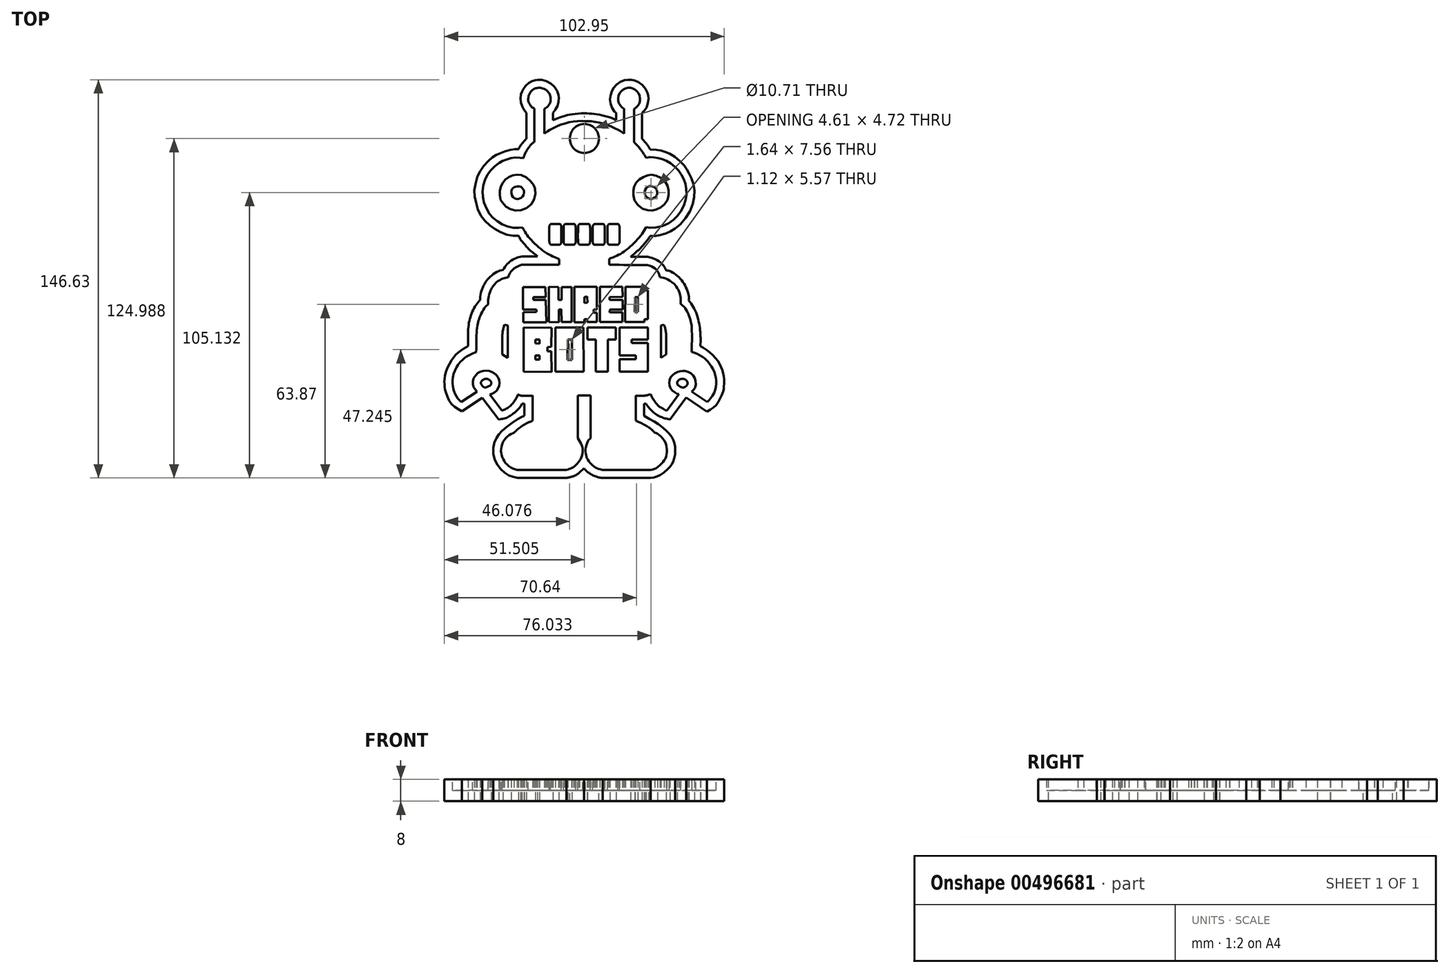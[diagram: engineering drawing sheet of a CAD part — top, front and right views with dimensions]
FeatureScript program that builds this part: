
annotation { "Feature Type Name" : "Feature", "Feature Type Description" : "" }
export const myFeature = defineFeature(function(context is Context, id is Id, definition is map)
    precondition{}
    {
        {
            var Q0;
            Q0=qCreatedBy(makeId("Top.planeOp"),FACE);
            var sketch = newSketch(context, id + "F0", { "sketchPlane" : qUnion([Q0])});
            skFitSpline(sketch, "E0", {"points": [v(-33.72, 61.57) * mm, v(-33.68, 52.13) * mm], "startDerivative": vector(0.03, -9.44) * mm, "endDerivative": vector(0.03, -9.44) * mm});
            skFitSpline(sketch, "E1", {"points": [v(-33.68, 52.13) * mm, v(-35.22, 50.28) * mm, v(-36.11, 49.12) * mm, v(-36.6, 48.2) * mm], "startDerivative": vector(-3.96, -4.75) * mm, "endDerivative": vector(-1.58, -3.42) * mm});
            skFitSpline(sketch, "E2", {"points": [v(-36.6, 48.2) * mm, v(-37.9, 48.2) * mm, v(-40.15, 47.82) * mm, v(-43.12, 46.8) * mm, v(-45.14, 45.9) * mm, v(-47.1, 44.4) * mm, v(-49.93, 41.25) * mm, v(-51.74, 37.9) * mm, v(-52.83, 32.84) * mm, v(-52.37, 29.1) * mm, v(-50.76, 24.21) * mm, v(-47.66, 20.53) * mm, v(-44.54, 18.3) * mm, v(-40, 16.5) * mm, v(-36.6, 16.26) * mm], "startDerivative": vector(-28.12, 1) * mm, "endDerivative": vector(46, 0.52) * mm});
            skFitSpline(sketch, "E3", {"points": [v(-36.6, 16.26) * mm, v(-35.5, 14.47) * mm, v(-34.14, 12.88) * mm, v(-32.5, 11.09) * mm, v(-30.32, 9.35) * mm, v(-29.6, 8.67) * mm], "startDerivative": vector(5.06, -9.07) * mm, "endDerivative": vector(4.26, -4.36) * mm});
            skFitSpline(sketch, "E4", {"points": [v(-29.6, 8.67) * mm, v(-31.14, 8.67) * mm, v(-35.06, 8.67) * mm, v(-37.67, 8) * mm, v(-40.33, 6.3) * mm, v(-42.36, 3.73) * mm], "startDerivative": vector(-9, -0.16) * mm, "endDerivative": vector(-8.6, -12.76) * mm});
            skFitSpline(sketch, "E5", {"points": [v(-42.36, 3.73) * mm, v(-44.44, 3.04) * mm, v(-47.3, 0.96) * mm, v(-49.03, -1.36) * mm, v(-50.24, -4.07) * mm, v(-50.73, -6.97) * mm, v(-50.68, -7.26) * mm], "startDerivative": vector(-12.18, -3) * mm, "endDerivative": vector(1.14, -3.42) * mm});
            skFitSpline(sketch, "E6", {"points": [v(-50.68, -7.26) * mm, v(-52.5, -9.64) * mm, v(-54.12, -13.1) * mm, v(-55, -16.96) * mm, v(-55.11, -24.3) * mm], "startDerivative": vector(-9.2, -10.68) * mm, "endDerivative": vector(0.5, -24.66) * mm});
            skFitSpline(sketch, "E7", {"points": [v(-55.11, -24.3) * mm, v(-56.92, -25.36) * mm, v(-59.18, -27.03) * mm, v(-61.34, -29.66) * mm, v(-63.32, -33.87) * mm, v(-63.85, -37.1) * mm, v(-63.8, -38.97) * mm, v(-63.4, -41.27) * mm, v(-61.31, -45.51) * mm, v(-57.37, -48.31) * mm], "startDerivative": vector(-19.75, -10.94) * mm, "endDerivative": vector(31.85, -17.11) * mm});
            skFitSpline(sketch, "E8", {"points": [v(-57.37, -48.31) * mm, v(-50, -43.37) * mm], "startDerivative": vector(7.38, 4.94) * mm, "endDerivative": vector(7.38, 4.94) * mm});
            skFitSpline(sketch, "E9", {"points": [v(-50, -43.37) * mm, v(-43.89, -51.34) * mm], "startDerivative": vector(6.1, -7.97) * mm, "endDerivative": vector(6.1, -7.97) * mm});
            skFitSpline(sketch, "E10", {"points": [v(-43.89, -51.34) * mm, v(-40.84, -50.63) * mm, v(-38.2, -48.92) * mm, v(-35.96, -46.73) * mm, v(-35.35, -45.59) * mm], "startDerivative": vector(11.52, 1.79) * mm, "endDerivative": vector(2.53, 6.09) * mm});
            skFitSpline(sketch, "E11", {"points": [v(-35.35, -45.59) * mm, v(-34.41, -45.59) * mm], "startDerivative": vector(0.94, 0) * mm, "endDerivative": vector(0.94, 0) * mm});
            skFitSpline(sketch, "E12", {"points": [v(-34.41, -45.59) * mm, v(-34.41, -49.94) * mm], "startDerivative": vector(0, -4.35) * mm, "endDerivative": vector(0, -4.35) * mm});
            skFitSpline(sketch, "E13", {"points": [v(-34.41, -49.94) * mm, v(-35.94, -50.7) * mm, v(-41.53, -54.53) * mm, v(-44.22, -57.38) * mm, v(-45.67, -60.78) * mm, v(-45.44, -65.99) * mm, v(-42.51, -70.27) * mm, v(-39.44, -72.24) * mm, v(-36.49, -72.85) * mm, v(-35.04, -72.87) * mm, v(-19, -72.9) * mm], "startDerivative": vector(-20.15, -8.85) * mm, "endDerivative": vector(109.37, -0.31) * mm});
            skFitSpline(sketch, "E14", {"points": [v(-19, -72.9) * mm, v(-16.81, -72.36) * mm, v(-14.75, -71.35) * mm, v(-12.5, -69.3) * mm], "startDerivative": vector(7.07, 1.43) * mm, "endDerivative": vector(6.04, 6.2) * mm});
            skFitSpline(sketch, "E15", {"points": [v(-12.5, -69.3) * mm, v(-11.55, -70.31) * mm, v(-9.99, -71.47) * mm, v(-7.7, -72.5) * mm, v(-5.6, -72.9) * mm], "startDerivative": vector(4.23, -4.86) * mm, "endDerivative": vector(8.02, -0.98) * mm});
            skFitSpline(sketch, "E16", {"points": [v(-5.6, -72.9) * mm, v(12, -72.9) * mm], "startDerivative": vector(17.59, 0) * mm, "endDerivative": vector(17.59, 0) * mm});
            skFitSpline(sketch, "E17", {"points": [v(12, -72.9) * mm, v(13.93, -72.44) * mm, v(16.53, -71.16) * mm, v(19.02, -68.89) * mm, v(19.85, -67.74) * mm, v(20.67, -65.87) * mm, v(21.1, -62.88) * mm, v(20.89, -60.42) * mm, v(20.14, -58.37) * mm, v(18.17, -55.8) * mm, v(16.29, -54.24) * mm, v(14.59, -52.95) * mm, v(9.59, -49.94) * mm], "startDerivative": vector(26.18, 5.02) * mm, "endDerivative": vector(-46.44, 26.77) * mm});
            skFitSpline(sketch, "E18", {"points": [v(9.59, -49.94) * mm, v(9.59, -45.59) * mm], "startDerivative": vector(0, 4.35) * mm, "endDerivative": vector(0, 4.35) * mm});
            skFitSpline(sketch, "E19", {"points": [v(9.59, -45.59) * mm, v(10.38, -45.59) * mm], "startDerivative": vector(0.8, 0) * mm, "endDerivative": vector(0.8, 0) * mm});
            skFitSpline(sketch, "E20", {"points": [v(10.38, -45.59) * mm, v(11.08, -46.61) * mm, v(13.17, -48.8) * mm, v(15.38, -50.2) * mm, v(17.16, -50.87) * mm, v(19.2, -51.37) * mm], "startDerivative": vector(3.81, -6.07) * mm, "endDerivative": vector(10.55, -2.4) * mm});
            skFitSpline(sketch, "E21", {"points": [v(19.2, -51.37) * mm, v(25.12, -43.29) * mm], "startDerivative": vector(5.91, 8.08) * mm, "endDerivative": vector(5.91, 8.08) * mm});
            skFitSpline(sketch, "E22", {"points": [v(25.12, -43.29) * mm, v(32.76, -48.49) * mm], "startDerivative": vector(7.65, -5.2) * mm, "endDerivative": vector(7.65, -5.2) * mm});
            skFitSpline(sketch, "E23", {"points": [v(32.76, -48.49) * mm, v(35.65, -46.46) * mm, v(37.6, -43.7) * mm, v(38.83, -40.77) * mm, v(39.01, -39.42) * mm, v(39.06, -36.24) * mm, v(38.63, -34.01) * mm, v(37.74, -31.54) * mm, v(35.98, -28.83) * mm, v(33.14, -26.03) * mm, v(30.37, -24.36) * mm], "startDerivative": vector(28.34, 17) * mm, "endDerivative": vector(-26.52, 14.03) * mm});
            skFitSpline(sketch, "E24", {"points": [v(30.37, -24.36) * mm, v(30.37, -20.16) * mm, v(29.9, -16.05) * mm, v(28.19, -10.73) * mm, v(26.07, -7.55) * mm], "startDerivative": vector(0.3, 17.5) * mm, "endDerivative": vector(-9.61, 12.23) * mm});
            skFitSpline(sketch, "E25", {"points": [v(26.07, -7.55) * mm, v(26.07, -5.66) * mm, v(24.63, -1.87) * mm, v(22.13, 1.31) * mm, v(19.2, 3.23) * mm, v(17.72, 3.6) * mm], "startDerivative": vector(1.13, 10.6) * mm, "endDerivative": vector(-9.43, 1.47) * mm});
            skFitSpline(sketch, "E26", {"points": [v(17.72, 3.6) * mm, v(17.06, 4.92) * mm, v(15.08, 6.92) * mm, v(11.67, 8.35) * mm, v(10.38, 8.57) * mm, v(4.7, 8.6) * mm], "startDerivative": vector(-3.75, 8.68) * mm, "endDerivative": vector(-24, -0.23) * mm});
            skFitSpline(sketch, "E27", {"points": [v(4.7, 8.6) * mm, v(8.33, 11.8) * mm, v(10.84, 14.7) * mm, v(12, 16.27) * mm], "startDerivative": vector(9.53, 7.9) * mm, "endDerivative": vector(4.11, 5.82) * mm});
            skFitSpline(sketch, "E28", {"points": [v(12, 16.27) * mm, v(14.18, 16.27) * mm, v(17.72, 17.14) * mm, v(20, 18.3) * mm, v(23.53, 21.05) * mm, v(27.23, 26.97) * mm, v(28.15, 31.96) * mm, v(27.59, 36.22) * mm, v(26.07, 39.36) * mm, v(25.12, 41.05) * mm, v(22.96, 43.62) * mm, v(19.57, 46.2) * mm, v(17.1, 47.25) * mm, v(15.35, 47.8) * mm, v(11.83, 48.08) * mm], "startDerivative": vector(35.37, -2.49) * mm, "endDerivative": vector(-53.89, 2.23) * mm});
            skFitSpline(sketch, "E29", {"points": [v(11.83, 48.08) * mm, v(10.9, 49.6) * mm, v(8.85, 52.07) * mm], "startDerivative": vector(-1.86, 3.4) * mm, "endDerivative": vector(-3.99, 4.5) * mm});
            skFitSpline(sketch, "E30", {"points": [v(8.85, 52.07) * mm, v(8.85, 61.58) * mm], "startDerivative": vector(0, 9.51) * mm, "endDerivative": vector(0, 9.51) * mm});
            skFitSpline(sketch, "E31", {"points": [v(8.85, 61.58) * mm, v(9.59, 62.28) * mm, v(10.69, 63.95) * mm, v(11.22, 66.73) * mm, v(11.22, 67.75) * mm, v(10.97, 68.74) * mm, v(9.83, 70.86) * mm, v(7.66, 72.83) * mm, v(5.86, 73.58) * mm, v(4.42, 73.7) * mm, v(2.84, 73.68) * mm, v(0.76, 72.86) * mm, v(-1.17, 71.27) * mm, v(-2.1, 70.02) * mm, v(-2.85, 67.54) * mm, v(-2.84, 65.4) * mm, v(-2.08, 63.3) * mm, v(-0.89, 61.67) * mm, v(-0.65, 61.48) * mm], "startDerivative": vector(16.73, 15) * mm, "endDerivative": vector(8.62, -5.35) * mm});
            skFitSpline(sketch, "E32", {"points": [v(-0.65, 61.48) * mm, v(-0.65, 58.88) * mm], "startDerivative": vector(0, -2.6) * mm, "endDerivative": vector(0, -2.6) * mm});
            skFitSpline(sketch, "E33", {"points": [v(-0.65, 58.88) * mm, v(-1.8, 59.48) * mm, v(-4.22, 60.26) * mm, v(-6.7, 60.81) * mm, v(-8.97, 61.15) * mm, v(-11.06, 61.32) * mm, v(-13.75, 61.32) * mm, v(-16.78, 61.07) * mm, v(-19, 60.62) * mm, v(-23.92, 58.88) * mm], "startDerivative": vector(-12.9, 7.75) * mm, "endDerivative": vector(-34.54, -13.03) * mm});
            skFitSpline(sketch, "E34", {"points": [v(-23.92, 58.88) * mm, v(-23.92, 61.58) * mm], "startDerivative": vector(0, 2.7) * mm, "endDerivative": vector(0, 2.7) * mm});
            skFitSpline(sketch, "E35", {"points": [v(-23.92, 61.58) * mm, v(-22.7, 63.16) * mm, v(-21.92, 65.13) * mm, v(-21.75, 67.33) * mm, v(-21.87, 68.1) * mm, v(-22.94, 70.58) * mm, v(-24.88, 72.48) * mm, v(-27.77, 73.67) * mm, v(-29.73, 73.69) * mm, v(-30.35, 73.62) * mm, v(-31.84, 73.14) * mm, v(-33.15, 72.27) * mm, v(-34.72, 70.52) * mm, v(-35.38, 69.24) * mm, v(-35.6, 68.66) * mm, v(-35.84, 66.9) * mm, v(-35.6, 64.8) * mm, v(-34.72, 63.02) * mm, v(-33.72, 61.57) * mm], "startDerivative": vector(22.48, 25.93) * mm, "endDerivative": vector(18.46, -25.37) * mm});
            skFitSpline(sketch, "E36", {"points": [v(-28.94, 70.8) * mm, v(-30.65, 70.45) * mm, v(-32.54, 68.64) * mm, v(-32.91, 65.76) * mm, v(-31.71, 63.71) * mm, v(-30.72, 63.16) * mm], "startDerivative": vector(-9.3, -0.64) * mm, "endDerivative": vector(6.7, -2.61) * mm});
            skFitSpline(sketch, "E37", {"points": [v(-30.72, 63.16) * mm, v(-30.72, 50.92) * mm], "startDerivative": vector(0, -12.24) * mm, "endDerivative": vector(0, -12.24) * mm});
            skFitSpline(sketch, "E38", {"points": [v(-30.72, 50.92) * mm, v(-32.35, 49.42) * mm, v(-34.41, 46.09) * mm, v(-34.72, 44.94) * mm], "startDerivative": vector(-4.79, -3.63) * mm, "endDerivative": vector(-0.65, -4.05) * mm});
            skFitSpline(sketch, "E39", {"points": [v(-34.72, 44.94) * mm, v(-36.25, 45.06) * mm, v(-38.34, 45.05) * mm, v(-40.14, 44.7) * mm, v(-42.23, 43.92) * mm, v(-43.5, 43.27) * mm, v(-45.77, 41.53) * mm, v(-47.97, 38.8) * mm, v(-49.35, 35.75) * mm, v(-49.76, 32.17) * mm, v(-49.38, 28.88) * mm, v(-47.65, 25.05) * mm, v(-45.87, 22.78) * mm, v(-43.1, 20.82) * mm, v(-40.08, 19.59) * mm, v(-36.8, 19.18) * mm, v(-35.1, 19.36) * mm], "startDerivative": vector(-30.9, 2.83) * mm, "endDerivative": vector(31.04, 5) * mm});
            skFitSpline(sketch, "E40", {"points": [v(-35.1, 19.36) * mm, v(-34.1, 17.54) * mm, v(-32.76, 15.62) * mm, v(-29.65, 12.5) * mm, v(-26.33, 9.9) * mm, v(-23.42, 8.47) * mm, v(-21.58, 7.72) * mm], "startDerivative": vector(7.11, -13.17) * mm, "endDerivative": vector(12.76, -5.1) * mm});
            skFitSpline(sketch, "E41", {"points": [v(-21.58, 7.72) * mm, v(-21.58, 5.6) * mm], "startDerivative": vector(0, -2.12) * mm, "endDerivative": vector(0, -2.12) * mm});
            skFitSpline(sketch, "E42", {"points": [v(-21.58, 5.6) * mm, v(-35.46, 5.6) * mm], "startDerivative": vector(-13.89, 0) * mm, "endDerivative": vector(-13.89, 0) * mm});
            skFitSpline(sketch, "E43", {"points": [v(-35.46, 5.6) * mm, v(-36.5, 5.19) * mm, v(-38.44, 4.07) * mm, v(-39.97, 2.18) * mm, v(-40.38, 1) * mm], "startDerivative": vector(-4.69, -1.79) * mm, "endDerivative": vector(-1.31, -5.22) * mm});
            skFitSpline(sketch, "E44", {"points": [v(-40.38, 1) * mm, v(-41.88, 0.67) * mm, v(-44.2, -0.49) * mm, v(-45.75, -1.97) * mm, v(-46.8, -3.78) * mm, v(-47.72, -7) * mm, v(-47.77, -8.96) * mm], "startDerivative": vector(-10.18, -1.54) * mm, "endDerivative": vector(0.54, -10.9) * mm});
            skFitSpline(sketch, "E45", {"points": [v(-47.77, -8.96) * mm, v(-48.36, -9.47) * mm, v(-49.8, -11.4) * mm, v(-51, -14.02) * mm, v(-51.6, -16.04) * mm, v(-52, -19.09) * mm, v(-52.17, -26.66) * mm], "startDerivative": vector(-6.18, -4.65) * mm, "endDerivative": vector(-0.18, -30.7) * mm});
            skFitSpline(sketch, "E46", {"points": [v(-52.17, -26.66) * mm, v(-53.11, -26.84) * mm, v(-54.77, -27.67) * mm, v(-56.56, -28.79) * mm, v(-58.91, -31.32) * mm, v(-60.55, -35) * mm, v(-60.84, -38.6) * mm, v(-60.39, -40.82) * mm, v(-59.12, -43.39) * mm, v(-57.68, -44.86) * mm], "startDerivative": vector(-12.83, -1.29) * mm, "endDerivative": vector(14.75, -12.7) * mm});
            skFitSpline(sketch, "E47", {"points": [v(-57.68, -44.86) * mm, v(-51.83, -41.06) * mm], "startDerivative": vector(5.85, 3.8) * mm, "endDerivative": vector(5.85, 3.8) * mm});
            skFitSpline(sketch, "E48", {"points": [v(-51.83, -41.06) * mm, v(-52.93, -39.76) * mm, v(-53.44, -37.8) * mm, v(-52.75, -35.51) * mm, v(-51.1, -33.99) * mm, v(-49.26, -33.4) * mm, v(-47.22, -33.52) * mm, v(-45.64, -34.23) * mm, v(-44.27, -35.56) * mm, v(-43.6, -37.16) * mm, v(-43.73, -39.03) * mm, v(-44.46, -40.48) * mm, v(-45.82, -41.68) * mm, v(-47.1, -42.15) * mm], "startDerivative": vector(-16.34, 16.23) * mm, "endDerivative": vector(-19.37, -5.07) * mm});
            skFitSpline(sketch, "E49", {"points": [v(-47.1, -42.15) * mm, v(-42.73, -48.06) * mm], "startDerivative": vector(4.36, -5.9) * mm, "endDerivative": vector(4.36, -5.9) * mm});
            skFitSpline(sketch, "E50", {"points": [v(-42.73, -48.06) * mm, v(-40.8, -47.2) * mm, v(-38.7, -45.37) * mm, v(-37.32, -43.3) * mm, v(-36.8, -42.15) * mm], "startDerivative": vector(7.77, 2.8) * mm, "endDerivative": vector(2.25, 5.57) * mm});
            skFitSpline(sketch, "E51", {"points": [v(-36.8, -42.15) * mm, v(-35.46, -42.6) * mm, v(-33.64, -42.64) * mm, v(-31.42, -42.55) * mm], "startDerivative": vector(4.34, -1.91) * mm, "endDerivative": vector(6.08, 0.21) * mm});
            skFitSpline(sketch, "E52", {"points": [v(-31.42, -42.55) * mm, v(-31.42, -51.77) * mm], "startDerivative": vector(0, -9.22) * mm, "endDerivative": vector(0, -9.22) * mm});
            skFitSpline(sketch, "E53", {"points": [v(-31.42, -51.77) * mm, v(-32.92, -52.45) * mm, v(-35.1, -53.58) * mm, v(-38.22, -56.15) * mm], "startDerivative": vector(-5.43, -2.52) * mm, "endDerivative": vector(-7.66, -6.94) * mm});
            skFitSpline(sketch, "E54", {"points": [v(-38.22, -56.15) * mm, v(-39.52, -56.82) * mm, v(-41.01, -57.94) * mm, v(-42.4, -59.87) * mm, v(-43, -62.25) * mm, v(-42.93, -63.95) * mm, v(-42.11, -66.09) * mm, v(-41.04, -67.74) * mm, v(-39.04, -69.26) * mm, v(-37.16, -69.9) * mm], "startDerivative": vector(-13.73, -6.54) * mm, "endDerivative": vector(17.04, -4.21) * mm});
            skFitSpline(sketch, "E55", {"points": [v(-37.16, -69.9) * mm, v(-34.26, -69.9) * mm, v(-19.02, -69.9) * mm], "startDerivative": vector(7.67, 0) * mm, "endDerivative": vector(26.19, 0) * mm});
            skFitSpline(sketch, "E56", {"points": [v(-19.02, -69.9) * mm, v(-16.97, -69.18) * mm, v(-14.7, -67.3) * mm, v(-13.24, -64.66) * mm, v(-13.1, -61.49) * mm, v(-14.74, -58.3) * mm], "startDerivative": vector(11.94, 3.05) * mm, "endDerivative": vector(-9.32, 14.15) * mm});
            skFitSpline(sketch, "E57", {"points": [v(-14.74, -58.3) * mm, v(-14.74, -42.55) * mm], "startDerivative": vector(0, 15.74) * mm, "endDerivative": vector(0, 15.74) * mm});
            skFitSpline(sketch, "E58", {"points": [v(-14.74, -42.55) * mm, v(-10.08, -42.55) * mm], "startDerivative": vector(4.66, 0) * mm, "endDerivative": vector(4.66, 0) * mm});
            skFitSpline(sketch, "E59", {"points": [v(-10.08, -42.55) * mm, v(-10.08, -58.3) * mm], "startDerivative": vector(0, -15.74) * mm, "endDerivative": vector(0, -15.74) * mm});
            skFitSpline(sketch, "E60", {"points": [v(-10.08, -58.3) * mm, v(-10.88, -59.07) * mm, v(-11.83, -61.75) * mm, v(-11.8, -64.25) * mm, v(-11.17, -66.07) * mm, v(-9.63, -67.97) * mm, v(-7.95, -69.22) * mm, v(-5.78, -69.9) * mm], "startDerivative": vector(-7.92, -5.73) * mm, "endDerivative": vector(15.48, -3.67) * mm});
            skFitSpline(sketch, "E61", {"points": [v(-5.78, -69.9) * mm, v(11.98, -69.9) * mm], "startDerivative": vector(17.76, 0) * mm, "endDerivative": vector(17.76, 0) * mm});
            skFitSpline(sketch, "E62", {"points": [v(11.98, -69.9) * mm, v(14.1, -69.29) * mm, v(16.3, -67.3) * mm, v(17.68, -65.18) * mm, v(18, -62.04) * mm, v(17.02, -59.08) * mm, v(14.83, -56.76) * mm, v(13.6, -56.15) * mm], "startDerivative": vector(16.32, 2.56) * mm, "endDerivative": vector(-11.01, 4.2) * mm});
            skFitSpline(sketch, "E63", {"points": [v(13.6, -56.15) * mm, v(11.98, -54.69) * mm, v(9.91, -53.43) * mm, v(7.84, -52.33) * mm, v(6.62, -51.77) * mm], "startDerivative": vector(-6, 5.91) * mm, "endDerivative": vector(-5.64, 2.46) * mm});
            skFitSpline(sketch, "E64", {"points": [v(6.62, -51.77) * mm, v(6.62, -42.55) * mm], "startDerivative": vector(0, 9.22) * mm, "endDerivative": vector(0, 9.22) * mm});
            skFitSpline(sketch, "E65", {"points": [v(6.62, -42.55) * mm, v(9.97, -42.55) * mm, v(12.05, -42.04) * mm], "startDerivative": vector(6.4, -0.32) * mm, "endDerivative": vector(4.38, 1.4) * mm});
            skFitSpline(sketch, "E66", {"points": [v(12.05, -42.04) * mm, v(12.55, -43.17) * mm, v(13.58, -44.81) * mm, v(14.92, -46.32) * mm, v(16.06, -47.1) * mm, v(17.94, -48.1) * mm], "startDerivative": vector(2.65, -6.37) * mm, "endDerivative": vector(9.08, -4.7) * mm});
            skFitSpline(sketch, "E67", {"points": [v(17.94, -48.1) * mm, v(22.4, -42.04) * mm], "startDerivative": vector(4.45, 6.05) * mm, "endDerivative": vector(4.45, 6.05) * mm});
            skFitSpline(sketch, "E68", {"points": [v(22.4, -42.04) * mm, v(21.02, -41.49) * mm, v(19.35, -39.8) * mm, v(18.87, -37.36) * mm, v(20, -35.07) * mm, v(22.05, -33.77) * mm, v(24, -33.45) * mm, v(26.57, -34.2) * mm, v(28.35, -36.44) * mm, v(28.48, -39.3) * mm, v(27.18, -41.14) * mm], "startDerivative": vector(-17.1, 5.1) * mm, "endDerivative": vector(-16.19, -16.8) * mm});
            skFitSpline(sketch, "E69", {"points": [v(27.18, -41.14) * mm, v(32.83, -44.9) * mm], "startDerivative": vector(5.65, -3.76) * mm, "endDerivative": vector(5.65, -3.76) * mm});
            skFitSpline(sketch, "E70", {"points": [v(32.83, -44.9) * mm, v(34.52, -43.03) * mm, v(35.96, -39.96) * mm, v(36.08, -36.56) * mm, v(35.41, -33.77) * mm, v(33.68, -30.74) * mm, v(32.07, -28.96) * mm, v(30.1, -27.72) * mm, v(28, -26.75) * mm, v(27.18, -26.52) * mm], "startDerivative": vector(15.66, 15.4) * mm, "endDerivative": vector(-11.35, 2.38) * mm});
            skFitSpline(sketch, "E71", {"points": [v(27.18, -26.52) * mm, v(27.18, -17.77) * mm, v(26.95, -15.89) * mm, v(26.14, -13.15) * mm, v(24.47, -10.05) * mm, v(23.09, -8.78) * mm], "startDerivative": vector(0.37, 32.8) * mm, "endDerivative": vector(-9.41, 7.09) * mm});
            skFitSpline(sketch, "E72", {"points": [v(23.09, -8.78) * mm, v(23.09, -6.71) * mm, v(22.61, -4.54) * mm, v(21.2, -2) * mm, v(19.9, -0.87) * mm, v(17.83, 0.42) * mm, v(15.5, 1.02) * mm], "startDerivative": vector(0.46, 13.13) * mm, "endDerivative": vector(-13.83, 2.34) * mm});
            skFitSpline(sketch, "E73", {"points": [v(15.5, 1.02) * mm, v(15.13, 2.26) * mm, v(13.82, 4.07) * mm, v(11.2, 5.4) * mm, v(10.05, 5.52) * mm, v(-3.26, 5.6) * mm], "startDerivative": vector(-2.25, 9.5) * mm, "endDerivative": vector(-42.78, 0.3) * mm});
            skFitSpline(sketch, "E74", {"points": [v(-3.26, 5.6) * mm, v(-3.26, 7.82) * mm], "startDerivative": vector(0, 2.21) * mm, "endDerivative": vector(0, 2.21) * mm});
            skFitSpline(sketch, "E75", {"points": [v(-3.26, 7.82) * mm, v(-0.64, 8.82) * mm, v(3.35, 11.3) * mm, v(8.1, 16.02) * mm, v(10.34, 19.43) * mm], "startDerivative": vector(12.79, 4.28) * mm, "endDerivative": vector(7.93, 13.72) * mm});
            skFitSpline(sketch, "E76", {"points": [v(10.34, 19.43) * mm, v(12.05, 19.2) * mm, v(16.23, 19.83) * mm, v(19.93, 21.8) * mm, v(22.11, 23.91) * mm, v(24.2, 27.27) * mm, v(25.12, 30.84) * mm, v(25.12, 33.97) * mm, v(24.44, 36.46) * mm, v(23.36, 38.8) * mm, v(21.73, 40.9) * mm, v(19.35, 43) * mm, v(17.5, 44) * mm, v(15.5, 44.8) * mm, v(13.83, 45.07) * mm, v(12, 45.24) * mm, v(10.34, 44.95) * mm], "startDerivative": vector(29.98, -6.52) * mm, "endDerivative": vector(-32.88, -8.3) * mm});
            skFitSpline(sketch, "E77", {"points": [v(10.34, 44.95) * mm, v(9.45, 46.47) * mm, v(7.88, 48.65) * mm, v(5.87, 50.83) * mm], "startDerivative": vector(-2.86, 5.16) * mm, "endDerivative": vector(-5.63, 5.78) * mm});
            skFitSpline(sketch, "E78", {"points": [v(5.87, 50.83) * mm, v(5.87, 62.93) * mm], "startDerivative": vector(0, 12.1) * mm, "endDerivative": vector(0, 12.1) * mm});
            skFitSpline(sketch, "E79", {"points": [v(5.87, 62.93) * mm, v(7.2, 64.01) * mm, v(8.02, 65.48) * mm, v(8.1, 67.28) * mm, v(7.51, 68.94) * mm, v(6.08, 70.17) * mm, v(5.04, 70.74) * mm, v(3.37, 70.74) * mm, v(1.87, 70.07) * mm, v(0.67, 68.89) * mm, v(0.08, 67.2) * mm, v(0.14, 65.67) * mm, v(0.97, 64.1) * mm, v(2.32, 63.07) * mm], "startDerivative": vector(18.16, 12.76) * mm, "endDerivative": vector(18.74, -11.52) * mm});
            skFitSpline(sketch, "E80", {"points": [v(2.32, 63.07) * mm, v(2.32, 53.9) * mm], "startDerivative": vector(0, -9.17) * mm, "endDerivative": vector(0, -9.17) * mm});
            skFitSpline(sketch, "E81", {"points": [v(2.32, 53.9) * mm, v(1.44, 54.52) * mm, v(-0.4, 55.5) * mm, v(-4.37, 57.22) * mm, v(-8.96, 58.34) * mm, v(-12.01, 58.52) * mm, v(-15.62, 58.44) * mm, v(-20.59, 57.34) * mm, v(-24.41, 55.63) * mm, v(-27.14, 53.9) * mm], "startDerivative": vector(-12.9, 9.65) * mm, "endDerivative": vector(-23.98, -16.11) * mm});
            skFitSpline(sketch, "E82", {"points": [v(-27.14, 53.9) * mm, v(-27.14, 63.07) * mm], "startDerivative": vector(0, 9.17) * mm, "endDerivative": vector(0, 9.17) * mm});
            skFitSpline(sketch, "E83", {"points": [v(-27.14, 63.07) * mm, v(-26.2, 63.54) * mm, v(-25.15, 64.9) * mm, v(-24.76, 66.5) * mm, v(-25, 68.14) * mm, v(-25.97, 69.56) * mm, v(-27.68, 70.57) * mm, v(-28.94, 70.8) * mm], "startDerivative": vector(8, 2.9) * mm, "endDerivative": vector(-9.36, 0.8) * mm});
            skFitSpline(sketch, "E84", {"points": [v(-37.04, 34.5) * mm, v(-37.71, 34.37) * mm, v(-38.42, 34.08) * mm, v(-38.8, 33.58) * mm, v(-39.12, 32.97) * mm, v(-39.21, 32) * mm, v(-38.9, 30.91) * mm, v(-38.05, 30.14) * mm, v(-37.17, 29.8) * mm, v(-36.1, 30) * mm, v(-35.13, 30.68) * mm, v(-34.58, 31.9) * mm, v(-34.65, 32.91) * mm, v(-35.07, 33.72) * mm, v(-35.89, 34.4) * mm, v(-37.04, 34.5) * mm]});
            skFitSpline(sketch, "E85", {"points": [v(-37.17, 38.8) * mm, v(-38.7, 38.54) * mm, v(-40.1, 37.88) * mm, v(-41.32, 37.1) * mm, v(-42.3, 35.96) * mm, v(-43.04, 34.57) * mm, v(-43.4, 32.99) * mm, v(-43.52, 31.45) * mm, v(-43.22, 29.55) * mm, v(-43.14, 29.33) * mm, v(-41.79, 27.54) * mm, v(-39.71, 26.13) * mm, v(-37.63, 25.6) * mm, v(-35.01, 25.85) * mm, v(-32.4, 27.44) * mm, v(-30.83, 29.7) * mm, v(-30.4, 32.23) * mm, v(-30.67, 34.22) * mm, v(-31.49, 35.5) * mm, v(-33.2, 37.44) * mm, v(-35.59, 38.63) * mm, v(-37.17, 38.8) * mm]});
            skFitSpline(sketch, "E86", {"points": [v(12.05, 34.6) * mm, v(11.2, 34.44) * mm, v(10.03, 33.22) * mm, v(9.86, 32.2) * mm, v(10.27, 30.88) * mm, v(11.6, 29.92) * mm, v(13, 30) * mm, v(14.12, 30.9) * mm, v(14.48, 31.63) * mm, v(14.44, 32.78) * mm, v(14.06, 33.55) * mm, v(13.24, 34.28) * mm, v(12.05, 34.6) * mm]});
            skFitSpline(sketch, "E87", {"points": [v(12.33, 38.8) * mm, v(10.76, 38.5) * mm, v(8.67, 37.6) * mm, v(7, 36.17) * mm, v(6, 34.39) * mm, v(5.73, 32.85) * mm, v(5.76, 30.56) * mm, v(7.33, 27.55) * mm, v(10.52, 25.77) * mm, v(12.36, 25.63) * mm, v(14.24, 25.97) * mm, v(16.4, 27.24) * mm, v(18.18, 29.43) * mm, v(18.72, 31.86) * mm, v(18.45, 34.15) * mm, v(17.36, 36.27) * mm, v(14.96, 38.01) * mm, v(12.33, 38.8) * mm]});
            skFitSpline(sketch, "E88", {"points": [v(-24.66, 20.68) * mm, v(-21.53, 20.68) * mm], "startDerivative": vector(3.13, 0) * mm, "endDerivative": vector(3.13, 0) * mm});
            skFitSpline(sketch, "E89", {"points": [v(-21.53, 20.68) * mm, v(-21.2, 20.57) * mm, v(-20.97, 20.18) * mm, v(-20.85, 19.58) * mm, v(-20.84, 13.86) * mm], "startDerivative": vector(2.76, -0.3) * mm, "endDerivative": vector(-0.2, -13.4) * mm});
            skFitSpline(sketch, "E90", {"points": [v(-20.84, 13.86) * mm, v(-21.1, 13.28) * mm, v(-21.35, 13.06) * mm], "startDerivative": vector(-0.4, -1.15) * mm, "endDerivative": vector(-0.64, -0.43) * mm});
            skFitSpline(sketch, "E91", {"points": [v(-21.35, 13.06) * mm, v(-24.7, 13.06) * mm], "startDerivative": vector(-3.35, 0) * mm, "endDerivative": vector(-3.35, 0) * mm});
            skFitSpline(sketch, "E92", {"points": [v(-24.7, 13.06) * mm, v(-25.03, 13.31) * mm, v(-25.22, 13.86) * mm, v(-25.25, 19.78) * mm], "startDerivative": vector(-2.15, 1.42) * mm, "endDerivative": vector(0.2, 11.79) * mm});
            skFitSpline(sketch, "E93", {"points": [v(-25.25, 19.78) * mm, v(-25.03, 20.32) * mm, v(-24.66, 20.68) * mm], "startDerivative": vector(0.34, 1.14) * mm, "endDerivative": vector(0.84, 0.66) * mm});
            skFitSpline(sketch, "E94", {"points": [v(-19.4, 20.68) * mm, v(-16.27, 20.68) * mm], "startDerivative": vector(3.13, 0) * mm, "endDerivative": vector(3.13, 0) * mm});
            skFitSpline(sketch, "E95", {"points": [v(-16.27, 20.68) * mm, v(-15.93, 20.57) * mm, v(-15.7, 20.18) * mm, v(-15.58, 19.58) * mm, v(-15.57, 13.86) * mm], "startDerivative": vector(2.76, -0.3) * mm, "endDerivative": vector(-0.2, -13.4) * mm});
            skFitSpline(sketch, "E96", {"points": [v(-15.57, 13.86) * mm, v(-15.83, 13.28) * mm, v(-16.09, 13.06) * mm], "startDerivative": vector(-0.4, -1.15) * mm, "endDerivative": vector(-0.64, -0.43) * mm});
            skFitSpline(sketch, "E97", {"points": [v(-16.09, 13.06) * mm, v(-19.44, 13.06) * mm], "startDerivative": vector(-3.35, 0) * mm, "endDerivative": vector(-3.35, 0) * mm});
            skFitSpline(sketch, "E98", {"points": [v(-19.44, 13.06) * mm, v(-19.76, 13.31) * mm, v(-19.95, 13.86) * mm, v(-19.99, 19.78) * mm], "startDerivative": vector(-2.15, 1.42) * mm, "endDerivative": vector(0.2, 11.79) * mm});
            skFitSpline(sketch, "E99", {"points": [v(-19.99, 19.78) * mm, v(-19.76, 20.32) * mm, v(-19.4, 20.68) * mm], "startDerivative": vector(0.34, 1.14) * mm, "endDerivative": vector(0.84, 0.66) * mm});
            skFitSpline(sketch, "E100", {"points": [v(-14.08, 20.68) * mm, v(-10.95, 20.68) * mm], "startDerivative": vector(3.13, 0) * mm, "endDerivative": vector(3.13, 0) * mm});
            skFitSpline(sketch, "E101", {"points": [v(-10.95, 20.68) * mm, v(-10.61, 20.57) * mm, v(-10.4, 20.18) * mm, v(-10.27, 19.58) * mm, v(-10.26, 13.86) * mm], "startDerivative": vector(2.76, -0.3) * mm, "endDerivative": vector(-0.2, -13.4) * mm});
            skFitSpline(sketch, "E102", {"points": [v(-10.26, 13.86) * mm, v(-10.51, 13.28) * mm, v(-10.77, 13.06) * mm], "startDerivative": vector(-0.4, -1.15) * mm, "endDerivative": vector(-0.64, -0.43) * mm});
            skFitSpline(sketch, "E103", {"points": [v(-10.77, 13.06) * mm, v(-14.12, 13.06) * mm], "startDerivative": vector(-3.35, 0) * mm, "endDerivative": vector(-3.35, 0) * mm});
            skFitSpline(sketch, "E104", {"points": [v(-14.12, 13.06) * mm, v(-14.45, 13.31) * mm, v(-14.64, 13.86) * mm, v(-14.67, 19.78) * mm], "startDerivative": vector(-2.15, 1.42) * mm, "endDerivative": vector(0.2, 11.79) * mm});
            skFitSpline(sketch, "E105", {"points": [v(-14.67, 19.78) * mm, v(-14.45, 20.32) * mm, v(-14.08, 20.68) * mm], "startDerivative": vector(0.34, 1.14) * mm, "endDerivative": vector(0.84, 0.66) * mm});
            skFitSpline(sketch, "E106", {"points": [v(-8.7, 20.61) * mm, v(-5.56, 20.61) * mm], "startDerivative": vector(3.13, 0) * mm, "endDerivative": vector(3.13, 0) * mm});
            skFitSpline(sketch, "E107", {"points": [v(-5.56, 20.61) * mm, v(-5.22, 20.5) * mm, v(-5, 20.12) * mm, v(-4.88, 19.51) * mm, v(-4.87, 13.8) * mm], "startDerivative": vector(2.76, -0.3) * mm, "endDerivative": vector(-0.2, -13.4) * mm});
            skFitSpline(sketch, "E108", {"points": [v(-4.87, 13.8) * mm, v(-5.12, 13.21) * mm, v(-5.38, 13) * mm], "startDerivative": vector(-0.4, -1.15) * mm, "endDerivative": vector(-0.64, -0.43) * mm});
            skFitSpline(sketch, "E109", {"points": [v(-5.38, 13) * mm, v(-8.73, 13) * mm], "startDerivative": vector(-3.35, 0) * mm, "endDerivative": vector(-3.35, 0) * mm});
            skFitSpline(sketch, "E110", {"points": [v(-8.73, 13) * mm, v(-9.06, 13.25) * mm, v(-9.25, 13.8) * mm, v(-9.28, 19.71) * mm], "startDerivative": vector(-2.15, 1.42) * mm, "endDerivative": vector(0.2, 11.79) * mm});
            skFitSpline(sketch, "E111", {"points": [v(-9.28, 19.71) * mm, v(-9.06, 20.26) * mm, v(-8.7, 20.61) * mm], "startDerivative": vector(0.34, 1.14) * mm, "endDerivative": vector(0.84, 0.66) * mm});
            skFitSpline(sketch, "E112", {"points": [v(-3.26, 20.68) * mm, v(-0.13, 20.68) * mm], "startDerivative": vector(3.13, 0) * mm, "endDerivative": vector(3.13, 0) * mm});
            skFitSpline(sketch, "E113", {"points": [v(-0.13, 20.68) * mm, v(0.21, 20.57) * mm, v(0.43, 20.18) * mm, v(0.55, 19.58) * mm, v(0.56, 13.86) * mm], "startDerivative": vector(2.76, -0.3) * mm, "endDerivative": vector(-0.2, -13.4) * mm});
            skFitSpline(sketch, "E114", {"points": [v(0.56, 13.86) * mm, v(0.3, 13.28) * mm, v(0.05, 13.06) * mm], "startDerivative": vector(-0.4, -1.15) * mm, "endDerivative": vector(-0.64, -0.43) * mm});
            skFitSpline(sketch, "E115", {"points": [v(0.05, 13.06) * mm, v(-3.3, 13.06) * mm], "startDerivative": vector(-3.35, 0) * mm, "endDerivative": vector(-3.35, 0) * mm});
            skFitSpline(sketch, "E116", {"points": [v(-3.3, 13.06) * mm, v(-3.63, 13.31) * mm, v(-3.81, 13.86) * mm, v(-3.85, 19.78) * mm], "startDerivative": vector(-2.15, 1.42) * mm, "endDerivative": vector(0.2, 11.79) * mm});
            skFitSpline(sketch, "E117", {"points": [v(-3.85, 19.78) * mm, v(-3.63, 20.32) * mm, v(-3.26, 20.68) * mm], "startDerivative": vector(0.34, 1.14) * mm, "endDerivative": vector(0.84, 0.66) * mm});
            skFitSpline(sketch, "E118", {"points": [v(-41.79, -16.5) * mm, v(-40.57, -16.7) * mm], "startDerivative": vector(1.22, -0.2) * mm, "endDerivative": vector(1.22, -0.2) * mm});
            skFitSpline(sketch, "E119", {"points": [v(-40.57, -16.7) * mm, v(-40.57, -28.63) * mm], "startDerivative": vector(0, -11.94) * mm, "endDerivative": vector(0, -11.94) * mm});
            skFitSpline(sketch, "E120", {"points": [v(-40.57, -28.63) * mm, v(-42.5, -27.42) * mm], "startDerivative": vector(-1.94, 1.2) * mm, "endDerivative": vector(-1.94, 1.2) * mm});
            skFitSpline(sketch, "E121", {"points": [v(-42.5, -27.42) * mm, v(-42.5, -19.66) * mm, v(-41.79, -16.5) * mm], "startDerivative": vector(-0.56, 14.22) * mm, "endDerivative": vector(2.2, 7.14) * mm});
            skFitSpline(sketch, "E122", {"points": [v(-49.14, -39.55) * mm, v(-50.2, -38.66) * mm, v(-50.4, -37.54) * mm, v(-49.46, -36.6) * mm, v(-48.1, -36.39) * mm, v(-47.01, -36.98) * mm, v(-46.61, -37.71) * mm, v(-46.81, -38.56) * mm, v(-47.55, -39.1) * mm, v(-49.14, -39.55) * mm]});
            skFitSpline(sketch, "E123", {"points": [v(24.28, -39.56) * mm, v(25.4, -38.69) * mm, v(25.65, -37.64) * mm, v(25.06, -36.84) * mm, v(24.14, -36.41) * mm, v(23.15, -36.41) * mm, v(22.3, -36.88) * mm, v(21.8, -37.6) * mm, v(22.1, -38.67) * mm, v(24.28, -39.56) * mm]});
            skFitSpline(sketch, "E124", {"points": [v(15.8, -16.7) * mm, v(15.8, -28.63) * mm], "startDerivative": vector(0.01, -11.94) * mm, "endDerivative": vector(0.01, -11.94) * mm});
            skFitSpline(sketch, "E125", {"points": [v(15.8, -28.63) * mm, v(17.73, -27.42) * mm], "startDerivative": vector(1.93, 1.2) * mm, "endDerivative": vector(1.93, 1.2) * mm});
            skFitSpline(sketch, "E126", {"points": [v(17.73, -27.42) * mm, v(17.6, -18.91) * mm, v(16.96, -16.5) * mm], "startDerivative": vector(0.31, 15.15) * mm, "endDerivative": vector(-2.1, 5.8) * mm});
            skFitSpline(sketch, "E127", {"points": [v(16.96, -16.5) * mm, v(15.8, -16.7) * mm], "startDerivative": vector(-1.16, -0.2) * mm, "endDerivative": vector(-1.16, -0.2) * mm});
            skLineSegment(sketch, "E128", {"start": v(-34.73, -2.58) * mm, "end": v(-26.64, -2.58) * mm});
            skLineSegment(sketch, "E129", {"start": v(-26.64, -2.58) * mm, "end": v(-26.55, -6.24) * mm});
            skLineSegment(sketch, "E130", {"start": v(-26.55, -6.24) * mm, "end": v(-31.2, -6.24) * mm});
            skLineSegment(sketch, "E131", {"start": v(-31.2, -6.24) * mm, "end": v(-31.18, -7.26) * mm});
            skLineSegment(sketch, "E132", {"start": v(-31.18, -7.26) * mm, "end": v(-26.55, -7.35) * mm});
            skLineSegment(sketch, "E133", {"start": v(-26.55, -7.35) * mm, "end": v(-26.37, -15.53) * mm});
            skLineSegment(sketch, "E134", {"start": v(-26.37, -15.53) * mm, "end": v(-34.82, -15.53) * mm});
            skLineSegment(sketch, "E135", {"start": v(-34.82, -15.53) * mm, "end": v(-34.82, -11.9) * mm});
            skLineSegment(sketch, "E136", {"start": v(-34.82, -11.9) * mm, "end": v(-30.04, -11.8) * mm});
            skLineSegment(sketch, "E137", {"start": v(-30.04, -11.8) * mm, "end": v(-30.06, -10.82) * mm});
            skLineSegment(sketch, "E138", {"start": v(-30.06, -10.82) * mm, "end": v(-34.9, -10.92) * mm});
            skLineSegment(sketch, "E139", {"start": v(-34.9, -10.92) * mm, "end": v(-34.9, -2.58) * mm});
            skLineSegment(sketch, "E140", {"start": v(-34.9, -2.58) * mm, "end": v(-34.73, -2.58) * mm});
            skLineSegment(sketch, "E141", {"start": v(-34.73, -17.52) * mm, "end": v(-34.73, -33.71) * mm});
            skLineSegment(sketch, "E142", {"start": v(-34.73, -33.71) * mm, "end": v(-24.42, -33.9) * mm});
            skLineSegment(sketch, "E143", {"start": v(-24.42, -33.9) * mm, "end": v(-24.59, -26.22) * mm});
            skLineSegment(sketch, "E144", {"start": v(-24.59, -26.22) * mm, "end": v(-25.93, -26.25) * mm});
            skLineSegment(sketch, "E145", {"start": v(-25.93, -26.25) * mm, "end": v(-25.96, -24.65) * mm});
            skLineSegment(sketch, "E146", {"start": v(-25.96, -24.65) * mm, "end": v(-24.59, -24.62) * mm});
            skLineSegment(sketch, "E147", {"start": v(-24.59, -24.62) * mm, "end": v(-24.38, -17.57) * mm});
            skLineSegment(sketch, "E148", {"start": v(-24.38, -17.57) * mm, "end": v(-34.73, -17.52) * mm});
            skLineSegment(sketch, "E149", {"start": v(-30.39, -21.86) * mm, "end": v(-30.39, -23.37) * mm});
            skLineSegment(sketch, "E150", {"start": v(-30.39, -23.37) * mm, "end": v(-28.83, -23.38) * mm});
            skLineSegment(sketch, "E151", {"start": v(-28.83, -23.38) * mm, "end": v(-28.83, -21.9) * mm});
            skLineSegment(sketch, "E152", {"start": v(-28.83, -21.9) * mm, "end": v(-30.39, -21.86) * mm});
            skLineSegment(sketch, "E153", {"start": v(-30.39, -27.78) * mm, "end": v(-28.87, -27.78) * mm});
            skLineSegment(sketch, "E154", {"start": v(-28.87, -27.78) * mm, "end": v(-28.87, -29.27) * mm});
            skLineSegment(sketch, "E155", {"start": v(-28.87, -29.27) * mm, "end": v(-30.39, -29.27) * mm});
            skLineSegment(sketch, "E156", {"start": v(-30.39, -29.27) * mm, "end": v(-30.39, -27.78) * mm});
            skLineSegment(sketch, "E157", {"start": v(-25.38, -2.48) * mm, "end": v(-25.38, -15.4) * mm});
            skLineSegment(sketch, "E158", {"start": v(-25.38, -15.4) * mm, "end": v(-21.75, -15.54) * mm});
            skLineSegment(sketch, "E159", {"start": v(-21.75, -15.54) * mm, "end": v(-21.75, -10.82) * mm});
            skLineSegment(sketch, "E160", {"start": v(-21.75, -10.82) * mm, "end": v(-20.83, -10.75) * mm});
            skLineSegment(sketch, "E161", {"start": v(-20.83, -10.75) * mm, "end": v(-20.68, -15.44) * mm});
            skLineSegment(sketch, "E162", {"start": v(-20.68, -15.44) * mm, "end": v(-17.06, -15.44) * mm});
            skLineSegment(sketch, "E163", {"start": v(-17.06, -15.44) * mm, "end": v(-17.06, -2.63) * mm});
            skLineSegment(sketch, "E164", {"start": v(-17.06, -2.63) * mm, "end": v(-20.68, -2.63) * mm});
            skLineSegment(sketch, "E165", {"start": v(-20.68, -2.63) * mm, "end": v(-20.68, -7.37) * mm});
            skLineSegment(sketch, "E166", {"start": v(-20.68, -7.37) * mm, "end": v(-21.85, -7.27) * mm});
            skLineSegment(sketch, "E167", {"start": v(-21.85, -7.27) * mm, "end": v(-21.85, -2.58) * mm});
            skLineSegment(sketch, "E168", {"start": v(-21.85, -2.58) * mm, "end": v(-25.38, -2.48) * mm});
            skLineSegment(sketch, "E169", {"start": v(-16.04, -2.48) * mm, "end": v(-16.04, -15.54) * mm});
            skLineSegment(sketch, "E170", {"start": v(-16.04, -15.54) * mm, "end": v(-12.38, -15.54) * mm});
            skLineSegment(sketch, "E171", {"start": v(-12.38, -15.54) * mm, "end": v(-12.36, -14.42) * mm});
            skLineSegment(sketch, "E172", {"start": v(-12.36, -14.42) * mm, "end": v(-11.38, -14.38) * mm});
            skLineSegment(sketch, "E173", {"start": v(-11.38, -14.38) * mm, "end": v(-11.35, -15.47) * mm});
            skLineSegment(sketch, "E174", {"start": v(-11.35, -15.47) * mm, "end": v(-7.74, -15.47) * mm});
            skLineSegment(sketch, "E175", {"start": v(-7.74, -15.47) * mm, "end": v(-7.78, -11.97) * mm});
            skLineSegment(sketch, "E176", {"start": v(-7.78, -11.97) * mm, "end": v(-8.97, -12) * mm});
            skLineSegment(sketch, "E177", {"start": v(-8.97, -12) * mm, "end": v(-8.96, -10.9) * mm});
            skLineSegment(sketch, "E178", {"start": v(-8.96, -10.9) * mm, "end": v(-7.8, -10.8) * mm});
            skLineSegment(sketch, "E179", {"start": v(-7.8, -10.8) * mm, "end": v(-7.8, -2.48) * mm});
            skLineSegment(sketch, "E180", {"start": v(-7.8, -2.48) * mm, "end": v(-16.04, -2.48) * mm});
            skLineSegment(sketch, "E181", {"start": v(-12.4, -6.24) * mm, "end": v(-12.4, -8.47) * mm});
            skLineSegment(sketch, "E182", {"start": v(-12.4, -8.47) * mm, "end": v(-11.2, -8.39) * mm});
            skLineSegment(sketch, "E183", {"start": v(-11.2, -8.39) * mm, "end": v(-11.31, -6.08) * mm});
            skLineSegment(sketch, "E184", {"start": v(-11.31, -6.08) * mm, "end": v(-12.4, -6.24) * mm});
            skLineSegment(sketch, "E185", {"start": v(-22.97, -17.52) * mm, "end": v(-12.72, -17.52) * mm});
            skLineSegment(sketch, "E186", {"start": v(-12.72, -17.52) * mm, "end": v(-12.58, -33.7) * mm});
            skLineSegment(sketch, "E187", {"start": v(-12.58, -33.7) * mm, "end": v(-22.96, -33.7) * mm});
            skLineSegment(sketch, "E188", {"start": v(-22.96, -33.7) * mm, "end": v(-22.97, -17.52) * mm});
            skLineSegment(sketch, "E189", {"start": v(-18.5, -21.9) * mm, "end": v(-18.6, -29.36) * mm});
            skLineSegment(sketch, "E190", {"start": v(-18.6, -29.36) * mm, "end": v(-16.96, -29.43) * mm});
            skLineSegment(sketch, "E191", {"start": v(-16.96, -29.43) * mm, "end": v(-16.96, -21.86) * mm});
            skLineSegment(sketch, "E192", {"start": v(-16.96, -21.86) * mm, "end": v(-18.5, -21.9) * mm});
            skLineSegment(sketch, "E193", {"start": v(-11.18, -17.52) * mm, "end": v(-11.18, -21.9) * mm});
            skLineSegment(sketch, "E194", {"start": v(-11.18, -21.9) * mm, "end": v(-8.2, -21.9) * mm});
            skLineSegment(sketch, "E195", {"start": v(-8.2, -21.9) * mm, "end": v(-8.2, -33.7) * mm});
            skLineSegment(sketch, "E196", {"start": v(-8.2, -33.7) * mm, "end": v(-3.7, -33.7) * mm});
            skLineSegment(sketch, "E197", {"start": v(-3.7, -33.7) * mm, "end": v(-3.7, -21.9) * mm});
            skLineSegment(sketch, "E198", {"start": v(-3.7, -21.9) * mm, "end": v(-0.8, -21.91) * mm});
            skLineSegment(sketch, "E199", {"start": v(-0.8, -21.91) * mm, "end": v(-0.8, -17.52) * mm});
            skLineSegment(sketch, "E200", {"start": v(-0.8, -17.52) * mm, "end": v(-11.18, -17.52) * mm});
            skLineSegment(sketch, "E201", {"start": v(0.6, -17.52) * mm, "end": v(10.96, -17.52) * mm});
            skLineSegment(sketch, "E202", {"start": v(10.96, -17.52) * mm, "end": v(10.96, -21.9) * mm});
            skLineSegment(sketch, "E203", {"start": v(10.96, -21.9) * mm, "end": v(5.04, -21.9) * mm});
            skLineSegment(sketch, "E204", {"start": v(5.04, -21.9) * mm, "end": v(5.04, -23.25) * mm});
            skLineSegment(sketch, "E205", {"start": v(5.04, -23.25) * mm, "end": v(10.97, -23.25) * mm});
            skLineSegment(sketch, "E206", {"start": v(10.97, -23.25) * mm, "end": v(10.97, -33.76) * mm});
            skLineSegment(sketch, "E207", {"start": v(10.97, -33.76) * mm, "end": v(0.57, -33.76) * mm});
            skLineSegment(sketch, "E208", {"start": v(0.57, -33.76) * mm, "end": v(0.57, -29.14) * mm});
            skLineSegment(sketch, "E209", {"start": v(0.57, -29.14) * mm, "end": v(6.55, -29.14) * mm});
            skLineSegment(sketch, "E210", {"start": v(6.55, -29.14) * mm, "end": v(6.55, -27.78) * mm});
            skLineSegment(sketch, "E211", {"start": v(6.55, -27.78) * mm, "end": v(0.57, -27.78) * mm});
            skLineSegment(sketch, "E212", {"start": v(0.57, -27.78) * mm, "end": v(0.6, -17.52) * mm});
            skLineSegment(sketch, "E213", {"start": v(-6.6, -2.48) * mm, "end": v(-6.6, -15.47) * mm});
            skLineSegment(sketch, "E214", {"start": v(-6.6, -15.47) * mm, "end": v(1.66, -15.47) * mm});
            skLineSegment(sketch, "E215", {"start": v(1.66, -15.47) * mm, "end": v(1.66, -11.9) * mm});
            skLineSegment(sketch, "E216", {"start": v(1.66, -11.9) * mm, "end": v(-3.02, -11.89) * mm});
            skLineSegment(sketch, "E217", {"start": v(-3.02, -11.89) * mm, "end": v(-3, -10.86) * mm});
            skLineSegment(sketch, "E218", {"start": v(-3, -10.86) * mm, "end": v(1.7, -10.86) * mm});
            skLineSegment(sketch, "E219", {"start": v(1.7, -10.86) * mm, "end": v(1.7, -7.28) * mm});
            skLineSegment(sketch, "E220", {"start": v(1.7, -7.28) * mm, "end": v(-3.08, -7.28) * mm});
            skLineSegment(sketch, "E221", {"start": v(-3.08, -7.28) * mm, "end": v(-3.08, -6.24) * mm});
            skLineSegment(sketch, "E222", {"start": v(-3.08, -6.24) * mm, "end": v(1.7, -6.2) * mm});
            skLineSegment(sketch, "E223", {"start": v(1.7, -6.2) * mm, "end": v(1.67, -2.48) * mm});
            skLineSegment(sketch, "E224", {"start": v(1.67, -2.48) * mm, "end": v(-6.6, -2.48) * mm});
            skLineSegment(sketch, "E225", {"start": v(2.7, -2.48) * mm, "end": v(9.74, -2.51) * mm});
            skLineSegment(sketch, "E226", {"start": v(9.74, -2.51) * mm, "end": v(9.74, -3.84) * mm});
            skLineSegment(sketch, "E227", {"start": v(9.74, -3.84) * mm, "end": v(10.97, -3.8) * mm});
            skLineSegment(sketch, "E228", {"start": v(10.97, -3.8) * mm, "end": v(10.97, -14.38) * mm});
            skLineSegment(sketch, "E229", {"start": v(10.97, -14.38) * mm, "end": v(9.76, -14.38) * mm});
            skLineSegment(sketch, "E230", {"start": v(9.76, -14.38) * mm, "end": v(9.76, -15.47) * mm});
            skLineSegment(sketch, "E231", {"start": v(9.76, -15.47) * mm, "end": v(2.58, -15.47) * mm});
            skLineSegment(sketch, "E232", {"start": v(2.58, -15.47) * mm, "end": v(2.7, -2.48) * mm});
            skLineSegment(sketch, "E233", {"start": v(6.28, -6.24) * mm, "end": v(7.34, -6.24) * mm});
            skLineSegment(sketch, "E234", {"start": v(7.34, -6.24) * mm, "end": v(7.34, -11.8) * mm});
            skLineSegment(sketch, "E235", {"start": v(7.34, -11.8) * mm, "end": v(6.22, -11.8) * mm});
            skLineSegment(sketch, "E236", {"start": v(6.22, -11.8) * mm, "end": v(6.28, -6.24) * mm});
            skSolve(sketch);
        }
        {
            var Q0;
            Q0=makeQuery(id+"F0.imprint","IMPRINT",FACE,{"disambiguationData":[TD([[makeQuery(id+"F0.imprint","IMPRINT",EDGE,{"derivedFrom":sQuery(id+"F0.wireOp",EDGE,"E36")}),1.0]])]});
            extrude(context, id + "F1", {"entities" : qUnion([Q0]), "depth" : 4 * mm, "offsetDistance" : 25 * mm});
        }
        {
            var Q0;
            Q0=makeQuery(id+"F0.imprint","IMPRINT",FACE,{"disambiguationData":[TD([[makeQuery(id+"F0.imprint","IMPRINT",EDGE,{"derivedFrom":sQuery(id+"F0.wireOp",EDGE,"E0")}),1.0]])]});
            var Q1;
            Q1=makeQuery(id+"F0.imprint","IMPRINT",FACE,{"disambiguationData":[TD([[makeQuery(id+"F0.imprint","IMPRINT",EDGE,{"derivedFrom":sQuery(id+"F0.wireOp",EDGE,"E84")}),-1.0]])]});
            var Q2;
            Q2=makeQuery(id+"F0.imprint","IMPRINT",FACE,{"disambiguationData":[TD([[makeQuery(id+"F0.imprint","IMPRINT",EDGE,{"derivedFrom":sQuery(id+"F0.wireOp",EDGE,"E86")}),-1.0]])]});
            var Q3;
            Q3=makeQuery(id+"F0.imprint","IMPRINT",FACE,{"disambiguationData":[TD([[makeQuery(id+"F0.imprint","IMPRINT",EDGE,{"derivedFrom":sQuery(id+"F0.wireOp",EDGE,"E128")}),-1.0]])]});
            var Q4;
            Q4=makeQuery(id+"F0.imprint","IMPRINT",FACE,{"disambiguationData":[TD([[makeQuery(id+"F0.imprint","IMPRINT",EDGE,{"derivedFrom":sQuery(id+"F0.wireOp",EDGE,"E157")}),1.0]])]});
            var Q5;
            Q5=makeQuery(id+"F0.imprint","IMPRINT",FACE,{"disambiguationData":[TD([[makeQuery(id+"F0.imprint","IMPRINT",EDGE,{"derivedFrom":sQuery(id+"F0.wireOp",EDGE,"E169")}),1.0]])]});
            var Q6;
            Q6=makeQuery(id+"F0.imprint","IMPRINT",FACE,{"disambiguationData":[TD([[makeQuery(id+"F0.imprint","IMPRINT",EDGE,{"derivedFrom":sQuery(id+"F0.wireOp",EDGE,"E213")}),1.0]])]});
            var Q7;
            Q7=makeQuery(id+"F0.imprint","IMPRINT",FACE,{"disambiguationData":[TD([[makeQuery(id+"F0.imprint","IMPRINT",EDGE,{"derivedFrom":sQuery(id+"F0.wireOp",EDGE,"E225")}),-1.0]])]});
            var Q8;
            Q8=makeQuery(id+"F0.imprint","IMPRINT",FACE,{"disambiguationData":[TD([[makeQuery(id+"F0.imprint","IMPRINT",EDGE,{"derivedFrom":sQuery(id+"F0.wireOp",EDGE,"E201")}),-1.0]])]});
            var Q9;
            Q9=makeQuery(id+"F0.imprint","IMPRINT",FACE,{"disambiguationData":[TD([[makeQuery(id+"F0.imprint","IMPRINT",EDGE,{"derivedFrom":sQuery(id+"F0.wireOp",EDGE,"E193")}),1.0]])]});
            var Q10;
            Q10=makeQuery(id+"F0.imprint","IMPRINT",FACE,{"disambiguationData":[TD([[makeQuery(id+"F0.imprint","IMPRINT",EDGE,{"derivedFrom":sQuery(id+"F0.wireOp",EDGE,"E185")}),-1.0]])]});
            var Q11;
            Q11=makeQuery(id+"F0.imprint","IMPRINT",FACE,{"disambiguationData":[TD([[makeQuery(id+"F0.imprint","IMPRINT",EDGE,{"derivedFrom":sQuery(id+"F0.wireOp",EDGE,"E141")}),1.0]])]});
            var Q12;
            Q12=makeQuery(id+"F0.imprint","IMPRINT",FACE,{"disambiguationData":[TD([[makeQuery(id+"F0.imprint","IMPRINT",EDGE,{"derivedFrom":sQuery(id+"F0.wireOp",EDGE,"E88")}),-1.0]])]});
            var Q13;
            Q13=makeQuery(id+"F0.imprint","IMPRINT",FACE,{"disambiguationData":[TD([[makeQuery(id+"F0.imprint","IMPRINT",EDGE,{"derivedFrom":sQuery(id+"F0.wireOp",EDGE,"E94")}),-1.0]])]});
            var Q14;
            Q14=makeQuery(id+"F0.imprint","IMPRINT",FACE,{"disambiguationData":[TD([[makeQuery(id+"F0.imprint","IMPRINT",EDGE,{"derivedFrom":sQuery(id+"F0.wireOp",EDGE,"E100")}),-1.0]])]});
            var Q15;
            Q15=makeQuery(id+"F0.imprint","IMPRINT",FACE,{"disambiguationData":[TD([[makeQuery(id+"F0.imprint","IMPRINT",EDGE,{"derivedFrom":sQuery(id+"F0.wireOp",EDGE,"E106")}),-1.0]])]});
            var Q16;
            Q16=makeQuery(id+"F0.imprint","IMPRINT",FACE,{"disambiguationData":[TD([[makeQuery(id+"F0.imprint","IMPRINT",EDGE,{"derivedFrom":sQuery(id+"F0.wireOp",EDGE,"E112")}),-1.0]])]});
            var Q17;
            Q17=makeQuery(id+"F0.imprint","IMPRINT",FACE,{"disambiguationData":[TD([[makeQuery(id+"F0.imprint","IMPRINT",EDGE,{"derivedFrom":sQuery(id+"F0.wireOp",EDGE,"E124")}),1.0]])]});
            var Q18;
            Q18=makeQuery(id+"F0.imprint","IMPRINT",FACE,{"disambiguationData":[TD([[makeQuery(id+"F0.imprint","IMPRINT",EDGE,{"derivedFrom":sQuery(id+"F0.wireOp",EDGE,"E118")}),-1.0]])]});
            extrude(context, id + "F2", {"entities" : qUnion([Q0, Q1, Q2, Q3, Q4, Q5, Q6, Q7, Q8, Q9, Q10, Q11, Q12, Q13, Q14, Q15, Q16, Q17, Q18]), "operationType" : NewBodyOperationType.ADD, "depth" : 8 * mm, "offsetDistance" : 25 * mm});
        }
        {
            var Q0;
            Q0=makeQuery(id+"F1.opExtrude","CAP_FACE",FACE,{"disambiguationData":[OSD([sQuery(id+"F0.wireOp",EDGE,"E36"),sQuery(id+"F0.wireOp",EDGE,"E37"),sQuery(id+"F0.wireOp",EDGE,"E38"),sQuery(id+"F0.wireOp",EDGE,"E39"),sQuery(id+"F0.wireOp",EDGE,"E40"),sQuery(id+"F0.wireOp",EDGE,"E41"),sQuery(id+"F0.wireOp",EDGE,"E42"),sQuery(id+"F0.wireOp",EDGE,"E43"),sQuery(id+"F0.wireOp",EDGE,"E44"),sQuery(id+"F0.wireOp",EDGE,"E45"),sQuery(id+"F0.wireOp",EDGE,"E46"),sQuery(id+"F0.wireOp",EDGE,"E47"),sQuery(id+"F0.wireOp",EDGE,"E48"),sQuery(id+"F0.wireOp",EDGE,"E49"),sQuery(id+"F0.wireOp",EDGE,"E50"),sQuery(id+"F0.wireOp",EDGE,"E51"),sQuery(id+"F0.wireOp",EDGE,"E52"),sQuery(id+"F0.wireOp",EDGE,"E53"),sQuery(id+"F0.wireOp",EDGE,"E54"),sQuery(id+"F0.wireOp",EDGE,"E55"),sQuery(id+"F0.wireOp",EDGE,"E56"),sQuery(id+"F0.wireOp",EDGE,"E57"),sQuery(id+"F0.wireOp",EDGE,"E58"),sQuery(id+"F0.wireOp",EDGE,"E59"),sQuery(id+"F0.wireOp",EDGE,"E60"),sQuery(id+"F0.wireOp",EDGE,"E61"),sQuery(id+"F0.wireOp",EDGE,"E62"),sQuery(id+"F0.wireOp",EDGE,"E63"),sQuery(id+"F0.wireOp",EDGE,"E64"),sQuery(id+"F0.wireOp",EDGE,"E65"),sQuery(id+"F0.wireOp",EDGE,"E66"),sQuery(id+"F0.wireOp",EDGE,"E67"),sQuery(id+"F0.wireOp",EDGE,"E68"),sQuery(id+"F0.wireOp",EDGE,"E69"),sQuery(id+"F0.wireOp",EDGE,"E70"),sQuery(id+"F0.wireOp",EDGE,"E71"),sQuery(id+"F0.wireOp",EDGE,"E72"),sQuery(id+"F0.wireOp",EDGE,"E73"),sQuery(id+"F0.wireOp",EDGE,"E74"),sQuery(id+"F0.wireOp",EDGE,"E75"),sQuery(id+"F0.wireOp",EDGE,"E76"),sQuery(id+"F0.wireOp",EDGE,"E77"),sQuery(id+"F0.wireOp",EDGE,"E78"),sQuery(id+"F0.wireOp",EDGE,"E79"),sQuery(id+"F0.wireOp",EDGE,"E80"),sQuery(id+"F0.wireOp",EDGE,"E81"),sQuery(id+"F0.wireOp",EDGE,"E82"),sQuery(id+"F0.wireOp",EDGE,"E83"),sQuery(id+"F0.wireOp",EDGE,"E85"),sQuery(id+"F0.wireOp",EDGE,"E87"),sQuery(id+"F0.wireOp",EDGE,"E88"),sQuery(id+"F0.wireOp",EDGE,"E89"),sQuery(id+"F0.wireOp",EDGE,"E90"),sQuery(id+"F0.wireOp",EDGE,"E91"),sQuery(id+"F0.wireOp",EDGE,"E92"),sQuery(id+"F0.wireOp",EDGE,"E93"),sQuery(id+"F0.wireOp",EDGE,"E94"),sQuery(id+"F0.wireOp",EDGE,"E95"),sQuery(id+"F0.wireOp",EDGE,"E96"),sQuery(id+"F0.wireOp",EDGE,"E97"),sQuery(id+"F0.wireOp",EDGE,"E98"),sQuery(id+"F0.wireOp",EDGE,"E99"),sQuery(id+"F0.wireOp",EDGE,"E100"),sQuery(id+"F0.wireOp",EDGE,"E101"),sQuery(id+"F0.wireOp",EDGE,"E102"),sQuery(id+"F0.wireOp",EDGE,"E103"),sQuery(id+"F0.wireOp",EDGE,"E104"),sQuery(id+"F0.wireOp",EDGE,"E105"),sQuery(id+"F0.wireOp",EDGE,"E106"),sQuery(id+"F0.wireOp",EDGE,"E107"),sQuery(id+"F0.wireOp",EDGE,"E108"),sQuery(id+"F0.wireOp",EDGE,"E109"),sQuery(id+"F0.wireOp",EDGE,"E110"),sQuery(id+"F0.wireOp",EDGE,"E111"),sQuery(id+"F0.wireOp",EDGE,"E112"),sQuery(id+"F0.wireOp",EDGE,"E113"),sQuery(id+"F0.wireOp",EDGE,"E114"),sQuery(id+"F0.wireOp",EDGE,"E115"),sQuery(id+"F0.wireOp",EDGE,"E116"),sQuery(id+"F0.wireOp",EDGE,"E117"),sQuery(id+"F0.wireOp",EDGE,"E118"),sQuery(id+"F0.wireOp",EDGE,"E119"),sQuery(id+"F0.wireOp",EDGE,"E120"),sQuery(id+"F0.wireOp",EDGE,"E121"),sQuery(id+"F0.wireOp",EDGE,"E124"),sQuery(id+"F0.wireOp",EDGE,"E125"),sQuery(id+"F0.wireOp",EDGE,"E126"),sQuery(id+"F0.wireOp",EDGE,"E127"),sQuery(id+"F0.wireOp",EDGE,"E128"),sQuery(id+"F0.wireOp",EDGE,"E129"),sQuery(id+"F0.wireOp",EDGE,"E130"),sQuery(id+"F0.wireOp",EDGE,"E131"),sQuery(id+"F0.wireOp",EDGE,"E132"),sQuery(id+"F0.wireOp",EDGE,"E133"),sQuery(id+"F0.wireOp",EDGE,"E134"),sQuery(id+"F0.wireOp",EDGE,"E135"),sQuery(id+"F0.wireOp",EDGE,"E136"),sQuery(id+"F0.wireOp",EDGE,"E137"),sQuery(id+"F0.wireOp",EDGE,"E138"),sQuery(id+"F0.wireOp",EDGE,"E139"),sQuery(id+"F0.wireOp",EDGE,"E140"),sQuery(id+"F0.wireOp",EDGE,"E141"),sQuery(id+"F0.wireOp",EDGE,"E142"),sQuery(id+"F0.wireOp",EDGE,"E143"),sQuery(id+"F0.wireOp",EDGE,"E144"),sQuery(id+"F0.wireOp",EDGE,"E145"),sQuery(id+"F0.wireOp",EDGE,"E146"),sQuery(id+"F0.wireOp",EDGE,"E147"),sQuery(id+"F0.wireOp",EDGE,"E148"),sQuery(id+"F0.wireOp",EDGE,"E157"),sQuery(id+"F0.wireOp",EDGE,"E158"),sQuery(id+"F0.wireOp",EDGE,"E159"),sQuery(id+"F0.wireOp",EDGE,"E160"),sQuery(id+"F0.wireOp",EDGE,"E161"),sQuery(id+"F0.wireOp",EDGE,"E162"),sQuery(id+"F0.wireOp",EDGE,"E163"),sQuery(id+"F0.wireOp",EDGE,"E164"),sQuery(id+"F0.wireOp",EDGE,"E165"),sQuery(id+"F0.wireOp",EDGE,"E166"),sQuery(id+"F0.wireOp",EDGE,"E167"),sQuery(id+"F0.wireOp",EDGE,"E168"),sQuery(id+"F0.wireOp",EDGE,"E169"),sQuery(id+"F0.wireOp",EDGE,"E170"),sQuery(id+"F0.wireOp",EDGE,"E171"),sQuery(id+"F0.wireOp",EDGE,"E172"),sQuery(id+"F0.wireOp",EDGE,"E173"),sQuery(id+"F0.wireOp",EDGE,"E174"),sQuery(id+"F0.wireOp",EDGE,"E175"),sQuery(id+"F0.wireOp",EDGE,"E176"),sQuery(id+"F0.wireOp",EDGE,"E177"),sQuery(id+"F0.wireOp",EDGE,"E178"),sQuery(id+"F0.wireOp",EDGE,"E179"),sQuery(id+"F0.wireOp",EDGE,"E180"),sQuery(id+"F0.wireOp",EDGE,"E185"),sQuery(id+"F0.wireOp",EDGE,"E186"),sQuery(id+"F0.wireOp",EDGE,"E187"),sQuery(id+"F0.wireOp",EDGE,"E188"),sQuery(id+"F0.wireOp",EDGE,"E193"),sQuery(id+"F0.wireOp",EDGE,"E194"),sQuery(id+"F0.wireOp",EDGE,"E195"),sQuery(id+"F0.wireOp",EDGE,"E196"),sQuery(id+"F0.wireOp",EDGE,"E197"),sQuery(id+"F0.wireOp",EDGE,"E198"),sQuery(id+"F0.wireOp",EDGE,"E199"),sQuery(id+"F0.wireOp",EDGE,"E200"),sQuery(id+"F0.wireOp",EDGE,"E201"),sQuery(id+"F0.wireOp",EDGE,"E202"),sQuery(id+"F0.wireOp",EDGE,"E203"),sQuery(id+"F0.wireOp",EDGE,"E204"),sQuery(id+"F0.wireOp",EDGE,"E205"),sQuery(id+"F0.wireOp",EDGE,"E206"),sQuery(id+"F0.wireOp",EDGE,"E207"),sQuery(id+"F0.wireOp",EDGE,"E208"),sQuery(id+"F0.wireOp",EDGE,"E209"),sQuery(id+"F0.wireOp",EDGE,"E210"),sQuery(id+"F0.wireOp",EDGE,"E211"),sQuery(id+"F0.wireOp",EDGE,"E212"),sQuery(id+"F0.wireOp",EDGE,"E213"),sQuery(id+"F0.wireOp",EDGE,"E214"),sQuery(id+"F0.wireOp",EDGE,"E215"),sQuery(id+"F0.wireOp",EDGE,"E216"),sQuery(id+"F0.wireOp",EDGE,"E217"),sQuery(id+"F0.wireOp",EDGE,"E218"),sQuery(id+"F0.wireOp",EDGE,"E219"),sQuery(id+"F0.wireOp",EDGE,"E220"),sQuery(id+"F0.wireOp",EDGE,"E221"),sQuery(id+"F0.wireOp",EDGE,"E222"),sQuery(id+"F0.wireOp",EDGE,"E223"),sQuery(id+"F0.wireOp",EDGE,"E224"),sQuery(id+"F0.wireOp",EDGE,"E225"),sQuery(id+"F0.wireOp",EDGE,"E226"),sQuery(id+"F0.wireOp",EDGE,"E227"),sQuery(id+"F0.wireOp",EDGE,"E228"),sQuery(id+"F0.wireOp",EDGE,"E229"),sQuery(id+"F0.wireOp",EDGE,"E230"),sQuery(id+"F0.wireOp",EDGE,"E231"),sQuery(id+"F0.wireOp",EDGE,"E232")])],"isStart":false});
            var sketch = newSketch(context, id + "F3", { "sketchPlane" : qUnion([Q0])});
            skCircle(sketch, "E237", {"center": v(-12.35, 52.1) * mm, "radius": 5.35 * mm});
            skSolve(sketch);
        }
        {
            var Q0;
            Q0 = qSketchRegion(id + "F3", true);
            extrude(context, id + "F4", {"entities" : qUnion([Q0]), "operationType" : NewBodyOperationType.REMOVE, "oppositeDirection" : true, "depth" : 29 * mm, "offsetDistance" : 25 * mm});
        }
    });
